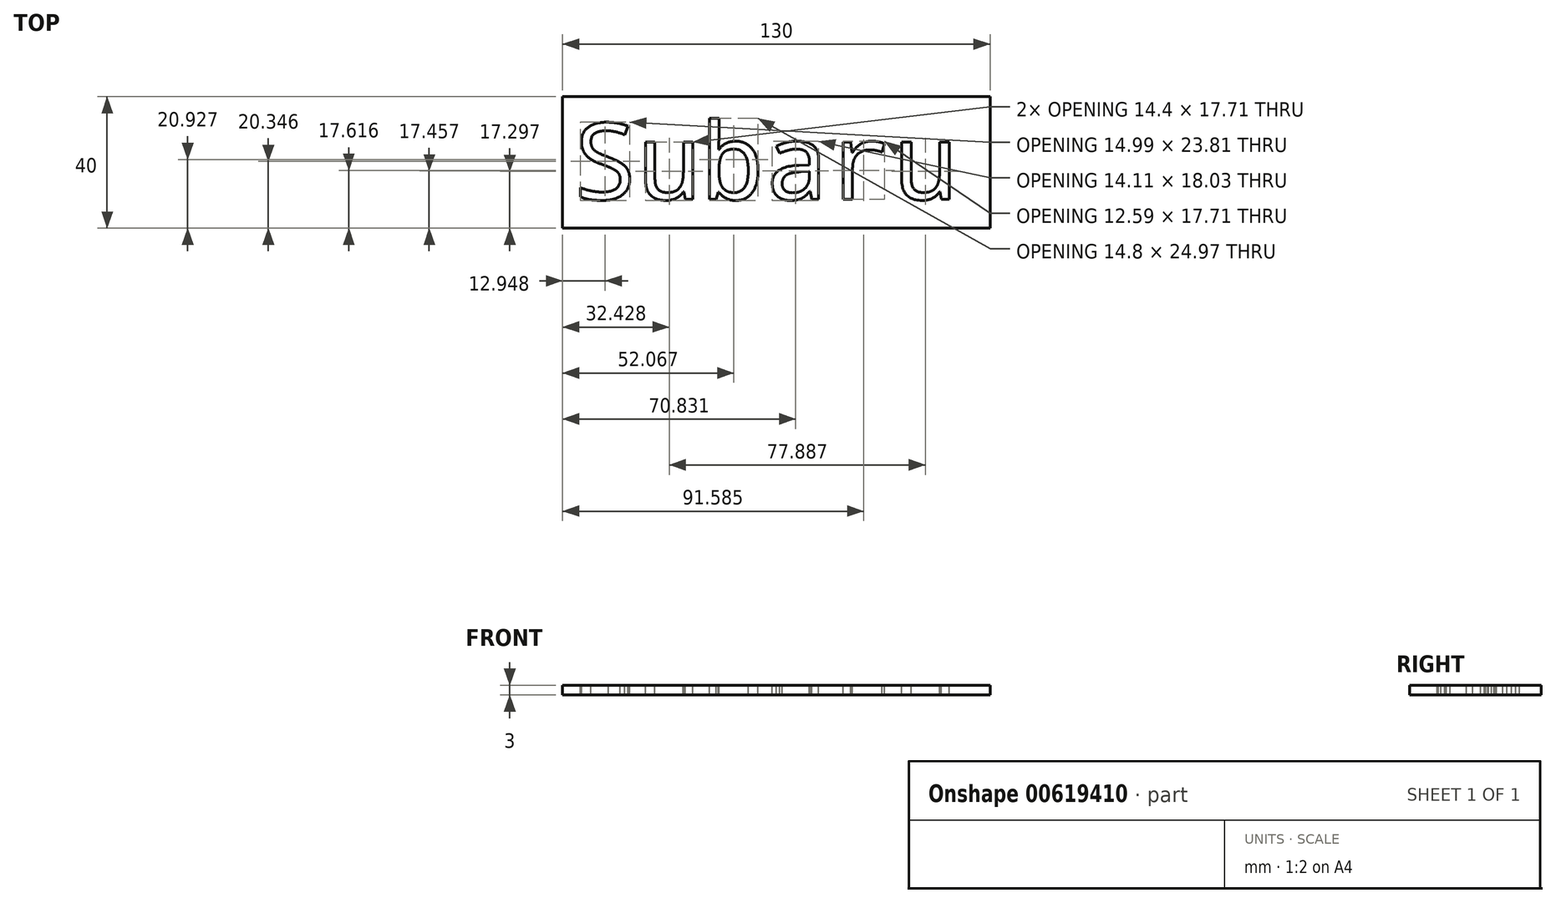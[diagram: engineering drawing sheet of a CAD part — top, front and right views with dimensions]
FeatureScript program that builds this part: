
annotation { "Feature Type Name" : "Feature", "Feature Type Description" : "" }
export const myFeature = defineFeature(function(context is Context, id is Id, definition is map)
    precondition{}
    {
        {
            var Q0;
            Q0=qCreatedBy(makeId("Top.planeOp"),FACE);
            var sketch = newSketch(context, id + "F0", { "sketchPlane" : qUnion([Q0])});
            skLineSegment(sketch, "E0", {"start": v(0, 0) * mm, "end": v(0, 40) * mm});
            skLineSegment(sketch, "E1", {"start": v(0, 40) * mm, "end": v(80, 40) * mm});
            skLineSegment(sketch, "E2", {"start": v(80, 40) * mm, "end": v(80, 0) * mm});
            skLineSegment(sketch, "E3", {"start": v(80, 0) * mm, "end": v(0, 0) * mm});
            skSolve(sketch);
        }
        {
            var Q0;
            Q0=makeQuery(id+"F0.imprint","IMPRINT",FACE,{"disambiguationData":[TD([[makeQuery(id+"F0.imprint","IMPRINT",EDGE,{"derivedFrom":sQuery(id+"F0.wireOp",EDGE,"E0")}),-1.0]])]});
            extrude(context, id + "F1", {"entities" : qUnion([Q0]), "depth" : 3 * mm, "offsetDistance" : 25 * mm});
        }
        {
            var Q0;
            Q0=makeQuery(id+"F1.opExtrude","CAP_FACE",FACE,{"disambiguationData":[OSD([sQuery(id+"F0.wireOp",EDGE,"E0"),sQuery(id+"F0.wireOp",EDGE,"E1"),sQuery(id+"F0.wireOp",EDGE,"E2"),sQuery(id+"F0.wireOp",EDGE,"E3")])],"isStart":false});
            var sketch = newSketch(context, id + "F2", { "sketchPlane" : qUnion([Q0])});
            skText(sketch, "E4", { "text": "Subaru", "fontName": "DroidSansMono.ttf"});
            const initialGuessF2  = {"E4": [0.00322, 0.00876, 1, 0, 0.02336]};
            skSetInitialGuess(sketch, initialGuessF2);
            skSolve(sketch);
        }
        {
            var Q0;
            Q0=makeQuery(id+"F1.opExtrude","SWEPT_FACE",FACE,{"disambiguationData":[OSD([sQuery(id+"F0.wireOp",EDGE,"E2")])]});
            extrude(context, id + "F3", {"entities" : qUnion([Q0]), "operationType" : NewBodyOperationType.ADD, "depth" : 50 * mm, "offsetDistance" : 25 * mm});
        }
        {
            var Q0;
            Q0 = qSketchRegion(id + "F2", true);
            extrude(context, id + "F4", {"entities" : qUnion([Q0]), "operationType" : NewBodyOperationType.REMOVE, "endBound" : BoundingType.THROUGH_ALL, "oppositeDirection" : true, "depth" : 25 * mm, "offsetDistance" : 25 * mm});
        }
    });
